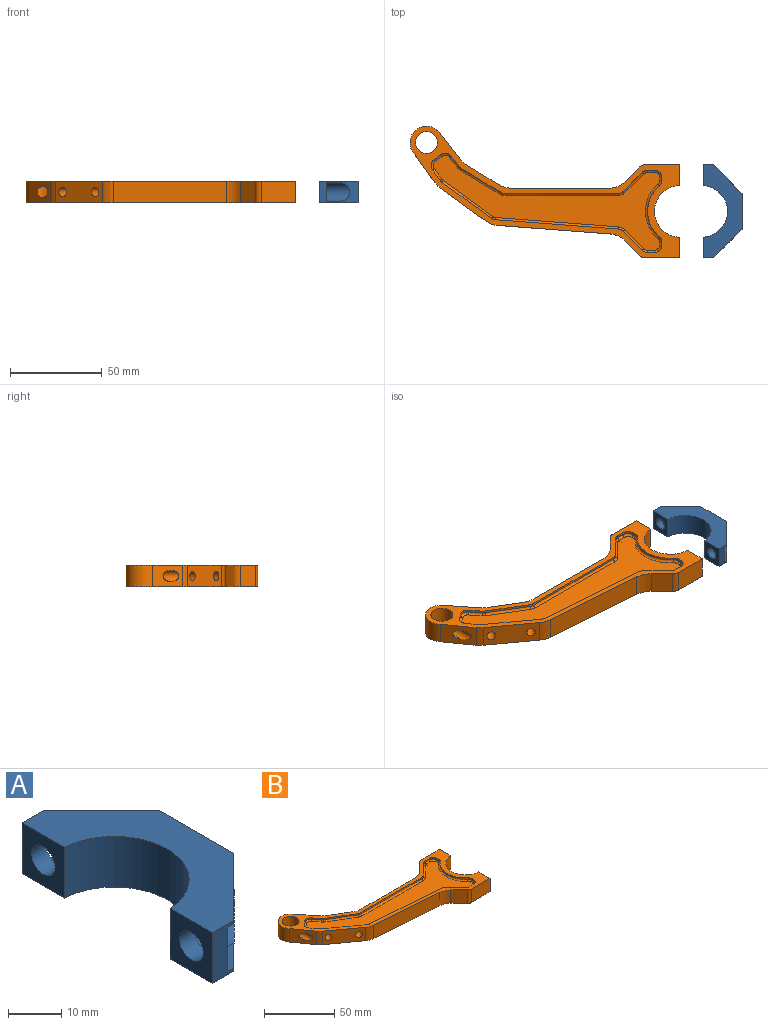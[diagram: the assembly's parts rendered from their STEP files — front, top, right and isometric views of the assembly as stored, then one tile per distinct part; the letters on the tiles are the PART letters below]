
ASSEMBLY  parts=2 mates=1
PART A: 22 faces, bbox 21.3x50.8x11.7 mm
  f0: plane 10.79x10.16mm, normal (1,0,0), area 66.8mm2, adj f1,f2,f3,f4,f5,f6
  f1: cylinder r=3.17mm len=6.35mm, axis (-1,0,0), area 39.9mm2, adj f0,f2,f7
  f2: cylinder r=3.17mm len=6.35mm, axis (-1,0,0), area 39.9mm2, adj f0,f1,f7
  f3: cylinder r=5.08mm len=12.58mm, axis (1,0,0), area 171mm2, adj f0,f4,f5,f9
  f4: plane 7.48x5.71mm, normal (0,0,-1), area 26.4mm2, adj f0,f3,f6,f9
  f5: plane 7.48x5.71mm, normal (0,0,1), area 26.4mm2, adj f0,f3,f6,f9
  f6: plane 11.7x5.78mm, normal (0,1,0), area 49.5mm2, adj f0,f4,f5,f7,f9,f14,f16
  f7: plane 11.7x11.32mm, normal (-1,0,0), area 100.8mm2, adj f1,f2,f6,f8,f14,f16
  f8: cylinder r=14.1mm len=28.16mm, axis (0,0,-1), area 500.7mm2, adj f7,f10,f14,f16
  f9: plane 15.47x15.47mm, normal (0.71,0.71,0), area 116.7mm2, adj f3,f4,f5,f6,f14,f15,f16
  f10: plane 11.7x11.32mm, normal (-1,0,0), area 100.8mm2, adj f8,f11,f12,f14,f16,f17
  f11: cylinder r=3.17mm len=6.35mm, axis (-1,0,0), area 39.9mm2, adj f10,f12,f18
  f12: cylinder r=3.17mm len=6.35mm, axis (-1,0,0), area 39.9mm2, adj f10,f11,f18
  f13: plane 7.46x5.71mm, normal (0,0,1), area 26.3mm2, adj f17,f18,f19,f21
  f14: plane 50.8x21.25mm, normal (0,0,-1), area 548.5mm2, adj f6,f7,f8,f9,f10,f15,f17,f19
  f15: plane 19.83x11.7mm, normal (1,0,0), area 232mm2, adj f9,f14,f16,f19
  f16: plane 50.8x21.25mm, normal (0,0,1), area 548.5mm2, adj f6,f7,f8,f9,f10,f15,f17,f19
  f17: plane 11.7x5.75mm, normal (0,-1,0), area 49.5mm2, adj f10,f13,f14,f16,f18,f19,f20
  f18: plane 10.79x10.16mm, normal (1,0,0), area 66.8mm2, adj f11,f12,f13,f17,f20,f21
  f19: plane 15.5x15.5mm, normal (0.71,-0.71,0), area 117.2mm2, adj f13,f14,f15,f16,f17,f20,f21
  f20: plane 7.46x5.71mm, normal (0,0,-1), area 26.3mm2, adj f17,f18,f19,f21
  f21: cylinder r=5.08mm len=12.54mm, axis (1,0,0), area 170.6mm2, adj f13,f18,f19,f20
PART B: 153 faces, bbox 147.8x72.7x12.5 mm
  f0: plane 123.67x51.84mm, normal (0,0,-1), area 1975.4mm2, adj f6,f7,f8,f9,f10,f11,f12,f13
  f1: cone r=0mm half-angle=59deg, axis (1,0,0), area 39.9mm2, adj f36
  f2: cone r=0mm half-angle=59deg, axis (1,0,0), area 39.9mm2, adj f37
  f3: plane 5x4.04mm, normal (-0.59,-0.81,0), area 19.6mm2, adj f38
  f4: plane 5x4.04mm, normal (-0.59,-0.81,0), area 19.6mm2, adj f39
  f5: plane 124.41x52.56mm, normal (0,0,1), area 1975.1mm2, adj f40,f41,f42,f43,f44,f45,f46,f47
  f6: torus R=5.2mm, axis (0,0,-1), area 4.5mm2, adj f0,f7,f35,f70
  f7: cylinder r=1.2mm len=61.71mm, axis (1,0,0), area 116.3mm2, adj f0,f6,f8,f71
  f8: torus R=5.2mm, axis (0,0,-1), area 6.6mm2, adj f0,f7,f9,f72
  f9: cylinder r=1.2mm len=11.21mm, axis (0.71,0.71,0), area 27.6mm2, adj f0,f8,f10,f73
  f10: torus R=2.8mm, axis (0,0,-1), area 5.3mm2, adj f0,f9,f11,f74
  f11: cylinder r=1.2mm len=3.94mm, axis (1,0,0), area 7.4mm2, adj f0,f10,f12,f75
  f12: torus R=2.8mm, axis (0,0,-1), area 10.6mm2, adj f0,f11,f13,f76
  f13: cylinder r=1.2mm len=1.56mm, axis (0,-1,0), area 2.9mm2, adj f0,f12,f14,f77
  f14: torus R=2.8mm, axis (0,0,-1), area 5.9mm2, adj f0,f13,f15,f78
  f15: torus R=19.2mm, axis (0,0,-1), area 30.3mm2, adj f0,f14,f16,f79
  f16: torus R=19.2mm, axis (0,0,-1), area 30.3mm2, adj f0,f15,f17,f79
  f17: torus R=2.8mm, axis (0,0,-1), area 5.9mm2, adj f0,f16,f18,f80
  f18: cylinder r=1.2mm len=1.56mm, axis (0,-1,0), area 2.9mm2, adj f0,f17,f19,f81
  f19: torus R=2.8mm, axis (0,0,-1), area 10.6mm2, adj f0,f18,f20,f82
  f20: cylinder r=1.2mm len=3.94mm, axis (-1,0,0), area 7.4mm2, adj f0,f19,f21,f83
  f21: torus R=2.8mm, axis (0,0,-1), area 5.3mm2, adj f0,f20,f22,f84
  f22: cylinder r=1.2mm len=11.24mm, axis (-0.71,0.71,0), area 27.7mm2, adj f0,f21,f23,f85
  f23: torus R=5.2mm, axis (0,0,-1), area 5.9mm2, adj f0,f22,f24,f86
  f24: cylinder r=1.2mm len=67.46mm, axis (-1,0.08,0), area 127.4mm2, adj f0,f23,f25,f87
  f25: torus R=2.8mm, axis (0,0,-1), area 3.7mm2, adj f0,f24,f26,f88
  f26: cylinder r=1.2mm len=27.8mm, axis (-0.81,0.59,0), area 63.2mm2, adj f0,f25,f27,f89
  f27: torus R=2.8mm, axis (0,0,-1), area 2.1mm2, adj f0,f26,f28,f90
  f28: cylinder r=1.2mm len=6.48mm, axis (-0.58,0.81,0), area 13.4mm2, adj f0,f27,f30,f91
  f29: torus R=2.8mm, axis (0,0,-1), area 6.2mm2, adj f0,f30,f31,f92
  f30: torus R=2.8mm, axis (0,0,-1), area 4.2mm2, adj f0,f28,f29,f92
  f31: cylinder r=1.2mm len=4.42mm, axis (0.8,0.6,0), area 8.7mm2, adj f0,f29,f32,f93
  f32: torus R=2.8mm, axis (0,0,-1), area 10.4mm2, adj f0,f31,f33,f94
  f33: cylinder r=1.2mm len=6.57mm, axis (0.62,-0.79,0), area 14mm2, adj f0,f32,f34,f95
  f34: torus R=5.2mm, axis (0,0,-1), area 3mm2, adj f0,f33,f35,f96
  f35: cylinder r=1.2mm len=22.35mm, axis (0.86,-0.52,0), area 47.9mm2, adj f0,f6,f34,f97
  f36: cylinder r=3.3mm len=18mm, axis (1,0,0), area 373.2mm2, adj f1,f101
  f37: cylinder r=3.3mm len=18mm, axis (1,0,0), area 373.2mm2, adj f2,f103
  f38: cylinder r=2.5mm len=11.03mm, axis (-0.59,-0.81,0), area 157.1mm2, adj f3,f113
  f39: cylinder r=2.5mm len=11.03mm, axis (-0.59,-0.81,0), area 157.1mm2, adj f4,f113
  f40: cylinder r=1.2mm len=6.57mm, axis (-0.62,0.79,0), area 14mm2, adj f5,f41,f67,f117
  f41: torus R=5.2mm, axis (0,0,1), area 3mm2, adj f5,f40,f42,f118
  f42: cylinder r=1.2mm len=22.35mm, axis (-0.86,0.52,0), area 47.9mm2, adj f5,f41,f43,f119
  f43: torus R=5.2mm, axis (0,0,1), area 4.5mm2, adj f5,f42,f44,f120
  f44: cylinder r=1.2mm len=61.71mm, axis (-1,0,0), area 116.3mm2, adj f5,f43,f45,f121
  f45: torus R=5.2mm, axis (0,0,1), area 6.6mm2, adj f5,f44,f46,f122
  f46: cylinder r=1.2mm len=11.21mm, axis (-0.71,-0.71,0), area 27.6mm2, adj f5,f45,f47,f123
  f47: torus R=2.8mm, axis (0,0,1), area 5.3mm2, adj f5,f46,f48,f124
  f48: cylinder r=1.2mm len=3.94mm, axis (-1,0,0), area 7.4mm2, adj f5,f47,f49,f125
  f49: torus R=2.8mm, axis (0,0,1), area 10.6mm2, adj f5,f48,f50,f126
  f50: cylinder r=1.2mm len=1.56mm, axis (0,1,0), area 2.9mm2, adj f5,f49,f51,f127
  f51: torus R=2.8mm, axis (0,0,1), area 5.9mm2, adj f5,f50,f52,f128
  f52: torus R=19.2mm, axis (0,0,1), area 60.6mm2, adj f5,f51,f53,f129
  f53: torus R=2.8mm, axis (0,0,1), area 5.9mm2, adj f5,f52,f54,f130
  f54: cylinder r=1.2mm len=1.56mm, axis (0,1,0), area 2.9mm2, adj f5,f53,f55,f131
  f55: torus R=2.8mm, axis (0,0,1), area 10.6mm2, adj f5,f54,f56,f132
  f56: cylinder r=1.2mm len=3.94mm, axis (1,0,0), area 7.4mm2, adj f5,f55,f57,f133
  f57: torus R=2.8mm, axis (0,0,1), area 5.3mm2, adj f5,f56,f58,f134
  f58: cylinder r=1.2mm len=11.24mm, axis (0.71,-0.71,0), area 27.7mm2, adj f5,f57,f59,f135
  f59: torus R=5.2mm, axis (0,0,1), area 5.9mm2, adj f5,f58,f60,f136
  f60: cylinder r=1.2mm len=67.46mm, axis (1,-0.08,0), area 127.4mm2, adj f5,f59,f61,f137
  f61: torus R=2.8mm, axis (0,0,1), area 3.7mm2, adj f5,f60,f62,f138
  f62: cylinder r=1.2mm len=27.8mm, axis (0.81,-0.59,0), area 63.2mm2, adj f5,f61,f63,f139
  f63: torus R=2.8mm, axis (0,0,1), area 2.1mm2, adj f5,f62,f64,f140
  f64: cylinder r=1.2mm len=6.48mm, axis (0.58,-0.81,0), area 13.4mm2, adj f5,f63,f65,f141
  f65: torus R=2.8mm, axis (0,0,1), area 10.4mm2, adj f5,f64,f66,f142
  f66: cylinder r=1.2mm len=4.42mm, axis (-0.8,-0.6,0), area 8.7mm2, adj f5,f65,f67,f143
  f67: torus R=2.8mm, axis (0,0,1), area 10.4mm2, adj f5,f40,f66,f144
  f68: cylinder r=3mm len=10.23mm, axis (0,1,0), area 67.4mm2, adj f69,f111,f145
  f69: cylinder r=3mm len=14.45mm, axis (0,1,0), area 117.8mm2, adj f68,f111,f145
  f70: cylinder r=4mm len=2.07mm, axis (0,0,-1), area 2.4mm2, adj f6,f71,f97,f147
  f71: plane 61.71x1.09mm, normal (0,-1,0), area 67mm2, adj f7,f70,f72,f147
  f72: cylinder r=4mm len=2.83mm, axis (0,0,-1), area 3.4mm2, adj f8,f71,f73,f147
  f73: plane 10.36x10.36mm, normal (0.71,-0.71,0), area 15.9mm2, adj f9,f72,f74,f147
  f74: cylinder r=4mm len=2.83mm, axis (0,0,1), area 3.4mm2, adj f10,f73,f75,f147
  f75: plane 3.94x1.09mm, normal (0,-1,0), area 4.3mm2, adj f11,f74,f76,f147
  f76: cylinder r=4mm len=4mm, axis (0,0,1), area 6.8mm2, adj f12,f75,f77,f147
  f77: plane 1.56x1.09mm, normal (-1,0,0), area 1.7mm2, adj f13,f76,f78,f147
  f78: cylinder r=4mm len=3.06mm, axis (0,0,-1), area 3.8mm2, adj f14,f77,f79,f147
  f79: cylinder r=18mm len=27.55mm, axis (0,0,-1), area 34.1mm2, adj f15,f16,f78,f80,f147
  f80: cylinder r=4mm len=3.06mm, axis (0,0,-1), area 3.8mm2, adj f17,f79,f81,f147
  f81: plane 1.56x1.09mm, normal (-1,0,0), area 1.7mm2, adj f18,f80,f82,f147
  f82: cylinder r=4mm len=4mm, axis (0,0,1), area 6.8mm2, adj f19,f81,f83,f147
  f83: plane 3.94x1.09mm, normal (0,1,0), area 4.3mm2, adj f20,f82,f84,f147
  f84: cylinder r=4mm len=2.83mm, axis (0,0,1), area 3.4mm2, adj f21,f83,f85,f147
  f85: plane 10.39x10.39mm, normal (0.71,0.71,0), area 16mm2, adj f22,f84,f86,f147
  f86: cylinder r=4mm len=2.53mm, axis (0,0,-1), area 3.1mm2, adj f23,f85,f87,f147
  f87: plane 67.37x5.11mm, normal (0.08,1,0), area 73.4mm2, adj f24,f86,f88,f147
  f88: cylinder r=4mm len=2.05mm, axis (0,0,1), area 2.4mm2, adj f25,f87,f89,f147
  f89: plane 27.09x19.75mm, normal (0.59,0.81,0), area 36.4mm2, adj f26,f88,f90,f147
  f90: cylinder r=4mm len=1.09mm, axis (0,0,1), area 1.4mm2, adj f27,f89,f91,f147
  f91: plane 5.78x4.13mm, normal (0.81,0.58,0), area 7.7mm2, adj f28,f90,f92,f147
  f92: cylinder r=4mm len=5.53mm, axis (0,0,1), area 6.7mm2, adj f29,f30,f91,f93,f147
  f93: plane 3.7x2.78mm, normal (0.6,-0.8,0), area 5mm2, adj f31,f92,f94,f147
  f94: cylinder r=4mm len=5.54mm, axis (0,0,1), area 6.7mm2, adj f32,f93,f95,f147
  f95: plane 5.83x4.59mm, normal (-0.79,-0.62,0), area 8.1mm2, adj f33,f94,f96,f147
  f96: cylinder r=4mm len=1.09mm, axis (0,0,-1), area 1.6mm2, adj f34,f95,f97,f147
  f97: plane 21.73x13.15mm, normal (-0.52,-0.86,0), area 27.6mm2, adj f35,f70,f96,f147
  f98: plane 11.7x8.38mm, normal (-0.71,-0.71,0), area 138.7mm2, adj f99,f116,f147,f149
  f99: cylinder r=4mm len=11.7mm, axis (0,0,-1), area 36.8mm2, adj f98,f100,f147,f149
  f100: plane 18.59x11.7mm, normal (0,-1,0), area 217.5mm2, adj f99,f101,f147,f149
  f101: plane 11.7x11.22mm, normal (1,0,0), area 97.1mm2, adj f36,f100,f102,f147,f149
  f102: cylinder r=14.2mm len=28.36mm, axis (0,0,-1), area 504.4mm2, adj f101,f103,f147,f149
  f103: plane 11.7x11.22mm, normal (1,0,0), area 97.1mm2, adj f37,f102,f104,f147,f149
  f104: plane 18.59x11.7mm, normal (0,1,0), area 217.5mm2, adj f103,f105,f147,f149
  f105: cylinder r=4mm len=11.7mm, axis (0,0,-1), area 36.8mm2, adj f104,f106,f147,f149
  f106: plane 11.7x8.01mm, normal (-0.71,0.71,0), area 132.6mm2, adj f105,f147,f148,f149
  f107: plane 17.39x11.7mm, normal (0.52,0.86,0), area 237.8mm2, adj f108,f146,f147,f149
  f108: cylinder r=12mm len=11.7mm, axis (0,0,1), area 50.5mm2, adj f107,f109,f147,f149
  f109: plane 15.37x12.1mm, normal (0.79,0.62,0), area 228.9mm2, adj f108,f110,f147,f149
  f110: cylinder r=9mm len=16.01mm, axis (0,0,-1), area 330.8mm2, adj f109,f111,f147,f149
  f111: plane 16.14x11.7mm, normal (-0.81,-0.58,0), area 183.5mm2, adj f68,f69,f110,f112,f147,f149
  f112: cylinder r=12mm len=11.7mm, axis (0,0,-1), area 44.9mm2, adj f111,f113,f147,f149
  f113: plane 25.29x18.44mm, normal (-0.59,-0.81,0), area 326.9mm2, adj f38,f39,f112,f114,f147,f149
  f114: cylinder r=12mm len=11.7mm, axis (0,0,-1), area 77.8mm2, adj f113,f115,f147,f149
  f115: plane 61.89x11.7mm, normal (-0.08,-1,0), area 726.2mm2, adj f114,f116,f147,f149
  f116: cylinder r=12mm len=11.7mm, axis (0,0,1), area 99.6mm2, adj f98,f115,f147,f149
  f117: plane 5.83x4.59mm, normal (-0.79,-0.62,0), area 8.1mm2, adj f40,f118,f144,f149
  f118: cylinder r=4mm len=1.09mm, axis (0,0,1), area 1.6mm2, adj f41,f117,f119,f149
  f119: plane 21.73x13.15mm, normal (-0.52,-0.86,0), area 27.6mm2, adj f42,f118,f120,f149
  f120: cylinder r=4mm len=2.07mm, axis (0,0,1), area 2.4mm2, adj f43,f119,f121,f149
  f121: plane 61.71x1.09mm, normal (0,-1,0), area 67mm2, adj f44,f120,f122,f149
  f122: cylinder r=4mm len=2.83mm, axis (0,0,1), area 3.4mm2, adj f45,f121,f123,f149
  f123: plane 10.36x10.36mm, normal (0.71,-0.71,0), area 15.9mm2, adj f46,f122,f124,f149
  f124: cylinder r=4mm len=2.83mm, axis (0,0,-1), area 3.4mm2, adj f47,f123,f125,f149
  f125: plane 3.94x1.09mm, normal (0,-1,0), area 4.3mm2, adj f48,f124,f126,f149
  f126: cylinder r=4mm len=4mm, axis (0,0,-1), area 6.8mm2, adj f49,f125,f127,f149
  f127: plane 1.56x1.09mm, normal (-1,0,0), area 1.7mm2, adj f50,f126,f128,f149
  f128: cylinder r=4mm len=3.06mm, axis (0,0,1), area 3.8mm2, adj f51,f127,f129,f149
  f129: cylinder r=18mm len=27.55mm, axis (0,0,1), area 34.1mm2, adj f52,f128,f130,f149
  f130: cylinder r=4mm len=3.06mm, axis (0,0,1), area 3.8mm2, adj f53,f129,f131,f149
  f131: plane 1.56x1.09mm, normal (-1,0,0), area 1.7mm2, adj f54,f130,f132,f149
  f132: cylinder r=4mm len=4mm, axis (0,0,-1), area 6.8mm2, adj f55,f131,f133,f149
  f133: plane 3.94x1.09mm, normal (0,1,0), area 4.3mm2, adj f56,f132,f134,f149
  f134: cylinder r=4mm len=2.83mm, axis (0,0,-1), area 3.4mm2, adj f57,f133,f135,f149
  f135: plane 10.39x10.39mm, normal (0.71,0.71,0), area 16mm2, adj f58,f134,f136,f149
  f136: cylinder r=4mm len=2.53mm, axis (0,0,1), area 3.1mm2, adj f59,f135,f137,f149
  f137: plane 67.37x5.11mm, normal (0.08,1,0), area 73.4mm2, adj f60,f136,f138,f149
  f138: cylinder r=4mm len=2.05mm, axis (0,0,-1), area 2.4mm2, adj f61,f137,f139,f149
  f139: plane 27.09x19.75mm, normal (0.59,0.81,0), area 36.4mm2, adj f62,f138,f140,f149
  f140: cylinder r=4mm len=1.09mm, axis (0,0,-1), area 1.4mm2, adj f63,f139,f141,f149
  f141: plane 5.78x4.13mm, normal (0.81,0.58,0), area 7.7mm2, adj f64,f140,f142,f149
  f142: cylinder r=4mm len=5.53mm, axis (0,0,-1), area 6.7mm2, adj f65,f141,f143,f149
  f143: plane 3.7x2.78mm, normal (0.6,-0.8,0), area 5mm2, adj f66,f142,f144,f149
  f144: cylinder r=4mm len=5.54mm, axis (0,0,-1), area 6.7mm2, adj f67,f117,f143,f149
  f145: cylinder r=6.03mm len=12.05mm, axis (0,0,-1), area 413.7mm2, adj f68,f69,f147,f149
  f146: cylinder r=12mm len=11.7mm, axis (0,0,1), area 76.4mm2, adj f107,f147,f149,f151
  f147: plane 146.94x71.93mm, normal (0,0,-1), area 1388.7mm2, adj f70,f71,f72,f73,f74,f75,f76,f77
  f148: cylinder r=12mm len=11.7mm, axis (0,0,1), area 110.3mm2, adj f106,f147,f149,f151
  f149: plane 146.94x71.93mm, normal (0,0,1), area 1388.7mm2, adj f98,f99,f100,f101,f102,f103,f104,f105
  f150: plane 5x5mm, normal (0,1,0), area 19.6mm2, adj f152
  f151: plane 54.09x11.7mm, normal (0,1,0), area 613.2mm2, adj f146,f147,f148,f149,f152
  f152: cylinder r=2.5mm len=10mm, axis (0,1,0), area 157.1mm2, adj f150,f151
PLACE A t=(57.91,52.83,12.14)mm
PLACE B t=(54.84,52.83,12.14)mm
MATE cylindrical B.f2 <-> A.f1  axis (1,0,0) through (54.09,72.58,17.99)mm
